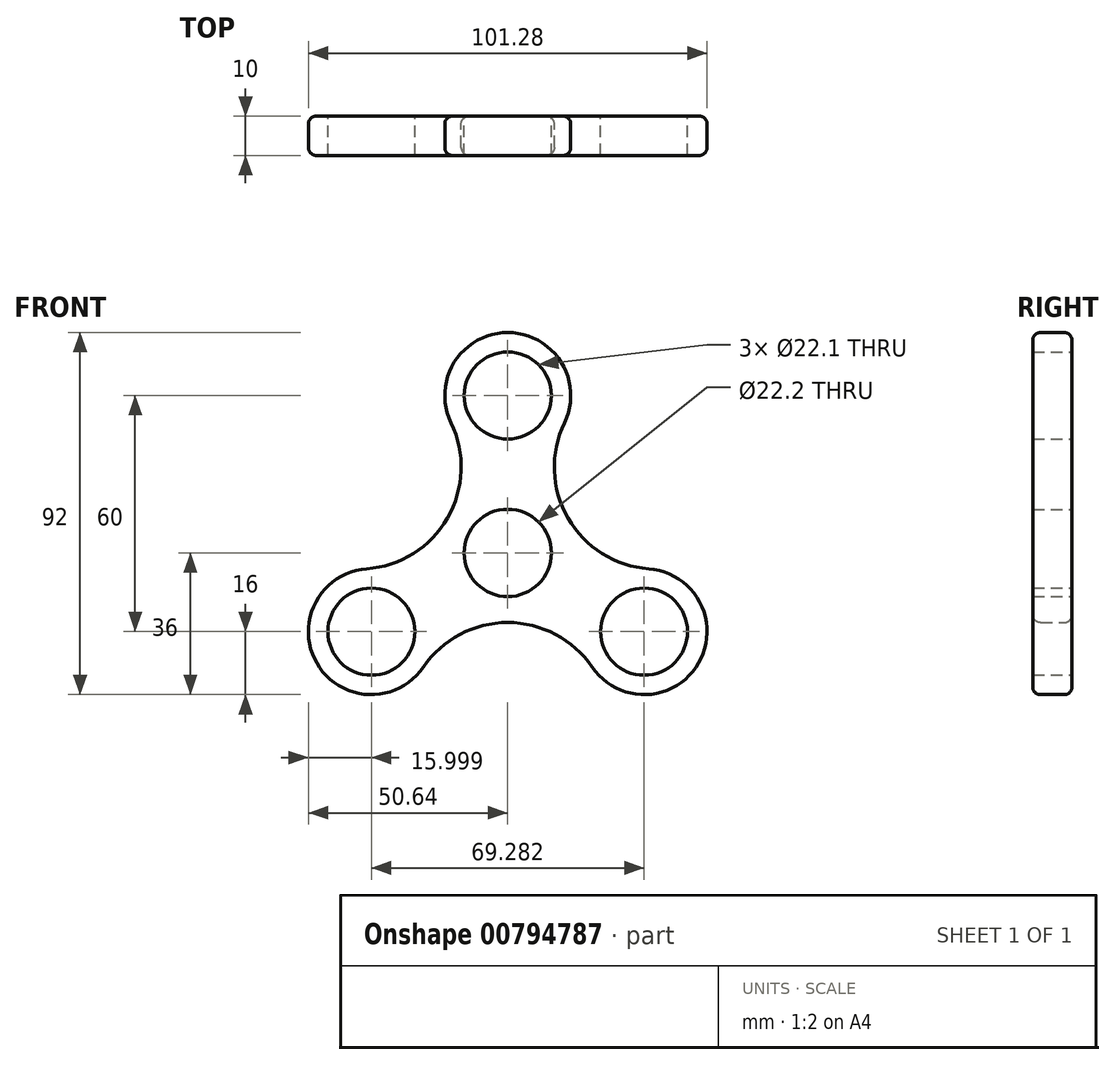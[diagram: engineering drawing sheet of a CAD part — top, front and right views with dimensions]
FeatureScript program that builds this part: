
annotation { "Feature Type Name" : "Feature", "Feature Type Description" : "" }
export const myFeature = defineFeature(function(context is Context, id is Id, definition is map)
    precondition{}
    {
        {
            var Q0;
            Q0=qCreatedBy(makeId("Front.planeOp"),FACE);
            var sketch = newSketch(context, id + "F0", { "sketchPlane" : qUnion([Q0])});
            skCircle(sketch, "E0", {"center": v(0, 0) * mm, "radius": 11.1 * mm});
            skCircle(sketch, "E1", {"center": v(0, 40) * mm, "radius": 11.05 * mm});
            skCircle(sketch, "E2.1.0", {"center": v(-34.64, -20) * mm, "radius": 11.05 * mm});
            skCircle(sketch, "E2.2.0", {"center": v(34.64, -20) * mm, "radius": 11.05 * mm});
            skCircle(sketch, "E3", {"center": v(0, 40) * mm, "radius": 16 * mm});
            skCircle(sketch, "E4.1.0", {"center": v(-34.64, -20) * mm, "radius": 16 * mm});
            skCircle(sketch, "E4.2.0", {"center": v(34.64, -20) * mm, "radius": 16 * mm});
            skLineSegment(sketch, "E5", {"start": v(0, 40) * mm, "end": v(34.64, -20) * mm, "construction": true});
            skLineSegment(sketch, "E6", {"start": v(8.26, 43.69) * mm, "end": v(42.34, -15.34) * mm, "construction": true});
            skArc(sketch, "E7", {"start": v(14.4, 33.04) * mm, "mid": v(15.3, 8.83) * mm, "end": v(35.82, -4.04) * mm});
            skArc(sketch, "E8.1.0", {"start": v(-35.82, -4.04) * mm, "mid": v(-15.3, 8.83) * mm, "end": v(-14.4, 33.04) * mm});
            skArc(sketch, "E8.2.0", {"start": v(21.41, -29) * mm, "mid": v(0, -17.67) * mm, "end": v(-21.41, -29) * mm});
            skSolve(sketch);
        }
        {
            var Q0;
            Q0=makeQuery(id+"F0.imprint","IMPRINT",FACE,{"disambiguationData":[TD([[makeQuery(id+"F0.imprint","IMPRINT",EDGE,{"derivedFrom":sQuery(id+"F0.wireOp",EDGE,"E1")}),-1.0]])]});
            var Q1;
            Q1=makeQuery(id+"F0.imprint","IMPRINT",FACE,{"disambiguationData":[TD([[makeQuery(id+"F0.imprint","IMPRINT",EDGE,{"derivedFrom":sQuery(id+"F0.wireOp",EDGE,"E0")}),-1.0]])]});
            var Q2;
            Q2=makeQuery(id+"F0.imprint","IMPRINT",FACE,{"disambiguationData":[TD([[makeQuery(id+"F0.imprint","IMPRINT",EDGE,{"derivedFrom":sQuery(id+"F0.wireOp",EDGE,"E2.1.0")}),-1.0]])]});
            var Q3;
            Q3=makeQuery(id+"F0.imprint","IMPRINT",FACE,{"disambiguationData":[TD([[makeQuery(id+"F0.imprint","IMPRINT",EDGE,{"derivedFrom":sQuery(id+"F0.wireOp",EDGE,"E2.2.0")}),-1.0]])]});
            extrude(context, id + "F1", {"entities" : qUnion([Q0, Q1, Q2, Q3]), "depth" : 10 * mm, "offsetDistance" : 25 * mm});
        }
        {
            var Q0;
            Q0=makeQuery(id+"F1.opExtrude","CAP_EDGE",EDGE,{"disambiguationData":[OSD([sQuery(id+"F0.wireOp",EDGE,"E8.1.0")])],"isStart":false});
            var Q1;
            Q1=makeQuery(id+"F1.opExtrude","CAP_EDGE",EDGE,{"disambiguationData":[OSD([sQuery(id+"F0.wireOp",EDGE,"E4.1.0")])],"isStart":false});
            var Q2;
            Q2=makeQuery(id+"F1.opExtrude","CAP_EDGE",EDGE,{"disambiguationData":[OSD([sQuery(id+"F0.wireOp",EDGE,"E8.2.0")])],"isStart":false});
            var Q3;
            Q3=makeQuery(id+"F1.opExtrude","CAP_EDGE",EDGE,{"disambiguationData":[OSD([sQuery(id+"F0.wireOp",EDGE,"E4.2.0")])],"isStart":false});
            var Q4;
            Q4=makeQuery(id+"F1.opExtrude","CAP_EDGE",EDGE,{"disambiguationData":[OSD([sQuery(id+"F0.wireOp",EDGE,"E7")])],"isStart":false});
            var Q5;
            Q5=makeQuery(id+"F1.opExtrude","CAP_EDGE",EDGE,{"disambiguationData":[OSD([sQuery(id+"F0.wireOp",EDGE,"E3")])],"isStart":false});
            fillet(context, id + "F2", {"entities" : qUnion([Q0, Q1, Q2, Q3, Q4, Q5]), "radius" : 2 * mm, "tangentPropagation" : true, "allowEdgeOverflow" : false});
        }
        {
            var Q0;
            Q0=makeQuery(id+"F1.opExtrude","CAP_EDGE",EDGE,{"disambiguationData":[OSD([sQuery(id+"F0.wireOp",EDGE,"E4.2.0")])],"isStart":true});
            var Q1;
            Q1=makeQuery(id+"F1.opExtrude","CAP_EDGE",EDGE,{"disambiguationData":[OSD([sQuery(id+"F0.wireOp",EDGE,"E8.2.0")])],"isStart":true});
            var Q2;
            Q2=makeQuery(id+"F1.opExtrude","CAP_EDGE",EDGE,{"disambiguationData":[OSD([sQuery(id+"F0.wireOp",EDGE,"E4.1.0")])],"isStart":true});
            var Q3;
            Q3=makeQuery(id+"F1.opExtrude","CAP_EDGE",EDGE,{"disambiguationData":[OSD([sQuery(id+"F0.wireOp",EDGE,"E8.1.0")])],"isStart":true});
            var Q4;
            Q4=makeQuery(id+"F1.opExtrude","CAP_EDGE",EDGE,{"disambiguationData":[OSD([sQuery(id+"F0.wireOp",EDGE,"E3")])],"isStart":true});
            var Q5;
            Q5=makeQuery(id+"F1.opExtrude","CAP_EDGE",EDGE,{"disambiguationData":[OSD([sQuery(id+"F0.wireOp",EDGE,"E7")])],"isStart":true});
            fillet(context, id + "F3", {"entities" : qUnion([Q0, Q1, Q2, Q3, Q4, Q5]), "radius" : 2 * mm, "tangentPropagation" : true, "allowEdgeOverflow" : false});
        }
    });
